# Revit family: Hydrablock 12-14-16
name_source: partatom
category: Attrezzatura meccanica
units: mm (PartAtom-declared; Revit-internal decimal feet)

## family parameters
Basato su piano di lavoro = No
Condiviso = No
Mantieni orientamento annotazione = No
Numero OmniClass = 23.75.00.00
Punto di calcolo locali = No
Quota connettore circolare = Usa diametro
Sempre verticale = Sì
Taglio con vuoti quando caricato = No
Tipo di parte = Normale
Titolo OmniClass = Climate Control (HVAC)

## types (6) — shared parameters
Air Flow = 6150 m³/h
Casing color = SB2014
Compressor = 1
Condensation = air
Depth = 405 mm  [stored 1.32874 ft]
Descrizione = High efficiency air cooled
Drain piping = 16 mm  [stored 0.0524934 ft]
Gas = R32
Height = 1414 mm
Installation = Outdoor installation
Machine material = Galvanized Steel
Produttore = Midea
Series = M-Thermal
URL = https://cac.midea.com
Water piping connections = 32 mm  [stored 0.104987 ft]
Width = 1404 mm
clearance access behind = 300 mm
clearance access front = 1500 mm
clearance access left = 600 mm
clearance access right = 600 mm
zero-valued in all types: Prospetto di default

## per-type parameters (varying)
| type | Cooling Power Input (EWT 23⁰C, LWT 18⁰C) | Cooling Power Input(EWT 12⁰C, LWT 7⁰C) | Cooling capacity (EWT 12⁰C, LWT 7⁰C) | Cooling capacity (EWT 23⁰C, LWT 18⁰C) | Heating Power Input (EWT 30⁰C, LWT 35⁰C) | Heating Power Input (EWT 40⁰C, LWT 45⁰C) | Heating capacity (EWT 30⁰C, LWT 35⁰C) | Heating capacity (EWT 40⁰C, LWT 45⁰C) | MOP (Maximum overcurrent protection) | Min cable selection (power wiring) | Minimum Circuit Amps | Modello | Net Weight | Power supply |
| Hydrablock 12 M | 3 kW | 4 kW | 11 kW | 12 kW | 3 kW | 4 kW | 12 kW | 12 kW | 30 A | 3×6 mm2 | 27 A | MHC-V12W/D2N8 | 158.00 kg | 220-240V 1N~50Hz |
| Hydrablock 14 M | 3 kW | 5 kW | 13 kW | 14 kW | 3 kW | 4 kW | 14 kW | 14 kW | 30 A | 3×6 mm2 | 27 A | MHC-V14W/D2N8 | 158.00 kg | 220-240V 1N~50Hz |
| Hydrablock 16 M | 4 kW | 5 kW | 14 kW | 16 kW | 4 kW | 5 kW | 16 kW | 16 kW | 30 A | 3×6 mm2 | 27 A | MHC-V16W/D2N8 | 158.00 kg | 220-240V 1N~50Hz |
| Hydrablock 12 T | 3 kW | 4 kW | 11 kW | 12 kW | 3 kW | 3 kW | 12 kW | 12 kW | 15 A | 5×4 mm2 | 11 A | MHC-V12W/D2RN8 | 172.00 kg | 380-415V 3N~50Hz |
| Hydrablock 14 T | 3 kW | 5 kW | 13 kW | 14 kW | 3 kW | 4 kW | 14 kW | 14 kW | 15 A | 5×4 mm2 | 11 A | MHC-V14W/D2RN8 | 172.00 kg | 380-415V 3N~50Hz |
| Hydrablock 16 T | 4 kW | 5 kW | 14 kW | 16 kW | 4 kW | 5 kW | 16 kW | 16 kW | 15 A | 5×4 mm2 | 11 A | MHC-V16W/D2RN8 | 172.00 kg | 380-415V 3N~50Hz |

note: [stored X ft] marks values corroborated as IEEE doubles in the binary element streams (Revit-internal decimal feet)

## geometry (parser evidence)
native form markers: Blend x2, Sweep x9
no freeform markers — native parametric forms only
